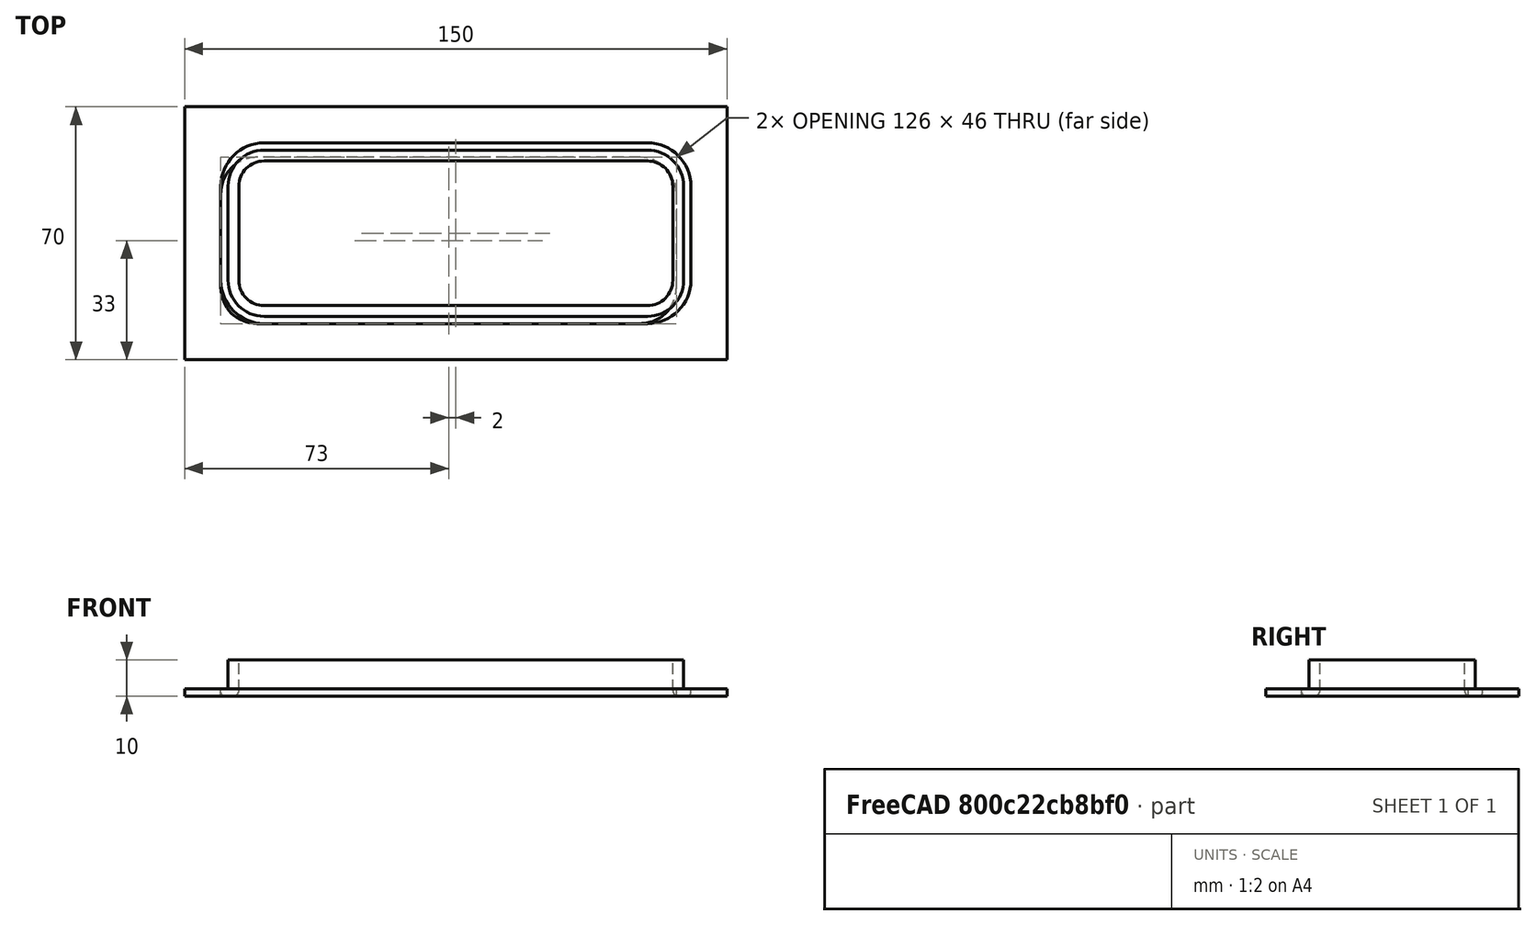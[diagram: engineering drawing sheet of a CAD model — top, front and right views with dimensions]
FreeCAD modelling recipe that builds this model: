
FCSTD DOCUMENT  (FreeCAD 1.0R39109 (Git))
Label: HandHandleBushing
License: All rights reserved
LicenseURL: https://en.wikipedia.org/wiki/All_rights_reserved
objects: Part::Fillet×6, Part::Box×5, Part::Cut×2, App::Part×2, Part::MultiFuse×1
note: 14 computed .brp shape members not serialized (recipe doc carries the construction recipe); baked Part::Feature solids carry a one-line shape summary decoded from their .brp

FEATURE [Part::Box] Box  label="inside_cut"
  AttacherType = Attacher::AttachEngine3D
  Height = 10
  Length = 120
  Width = 40
FEATURE [Part::Fillet] Fillet
  Base = -> Box
  EdgeLinks = -> Box [Edge1,Edge3,Edge5,Edge7]
  Edges = 4 edges r=7: [Edge1,Edge3,Edge5,Edge7]
  Placement = pos=(5,5,0) rot=(0,0,1;0rad)
FEATURE [Part::Box] Box001  label="Cube"
  AttacherType = Attacher::AttachEngine3D
  Height = 10
  Length = 126
  Width = 46
FEATURE [Part::Box] Box002  label="Cube001"
  AttacherType = Attacher::AttachEngine3D
  Height = 2
  Length = 130
  Width = 50
FEATURE [Part::Fillet] Fillet001
  Base = -> Box001
  EdgeLinks = -> Box001 [Edge1,Edge3,Edge5,Edge7]
  Edges = 4 edges r=10: [Edge1,Edge3,Edge5,Edge7]
  Placement = pos=(2,2,0) rot=(0,0,1;0rad)
FEATURE [Part::Fillet] Fillet002
  Base = -> Box002
  EdgeLinks = -> Box002 [Edge1,Edge3,Edge5,Edge7]
  Edges = 4 edges r=12: [Edge1,Edge3,Edge5,Edge7]
FEATURE [Part::MultiFuse] Fusion
  Shapes = -> [Fillet001,Fillet002]
FEATURE [Part::Cut] Cut
  Base = -> Fusion
  Tool = -> Fillet
FEATURE [Part::Fillet] Fillet003
  Base = -> Cut
  EdgeLinks = -> Cut [Edge41,Edge44,Edge46,Edge49,Edge50,Edge52,Edge54,Edge56]
  Edges = 8 edges r=1.5: [Edge41,Edge44,Edge46,Edge49,Edge50,Edge52,Edge54,Edge56]
FEATURE [Part::Fillet] Fillet004
  Base = -> Fillet003
  EdgeLinks = -> Fillet003 [Edge73,Edge74,Edge75,Edge76,Edge77,Edge78,Edge79,Edge80]
  Edges = 8 edges r=1: [Edge73,Edge74,Edge75,Edge76,Edge77,Edge78,Edge79,Edge80]
FEATURE [App::Part] Part  label="Handle"
  Group = -> [Fillet,Fillet002,Box,Fillet001,Box001,Fusion,Box002,Cut,Fillet003,Fillet004]
  Origin = -> Origin
FEATURE [Part::Box] Box003  label="Cube002"
  AttacherType = Attacher::AttachEngine3D
  Height = 10
  Length = 126
  Width = 46
FEATURE [Part::Box] Box004  label="Cube003"
  AttacherType = Attacher::AttachEngine3D
  Height = 2
  Length = 150
  Placement = pos=(-10,-10,0) rot=(0,0,1;0rad)
  Width = 70
FEATURE [Part::Fillet] Fillet005
  Base = -> Box003
  EdgeLinks = -> Box003 [Edge1,Edge3,Edge5,Edge7]
  Edges = 4 edges r=10: [Edge1,Edge3,Edge5,Edge7]
FEATURE [Part::Cut] Cut001
  Base = -> Box004
  Tool = -> Fillet005
FEATURE [App::Part] Part001  label="Template"
  Group = -> [Fillet005,Box003,Box004,Cut001]
  Origin = -> Origin001
  Placement = pos=(2,2,20) rot=(0,0,1;0rad)
